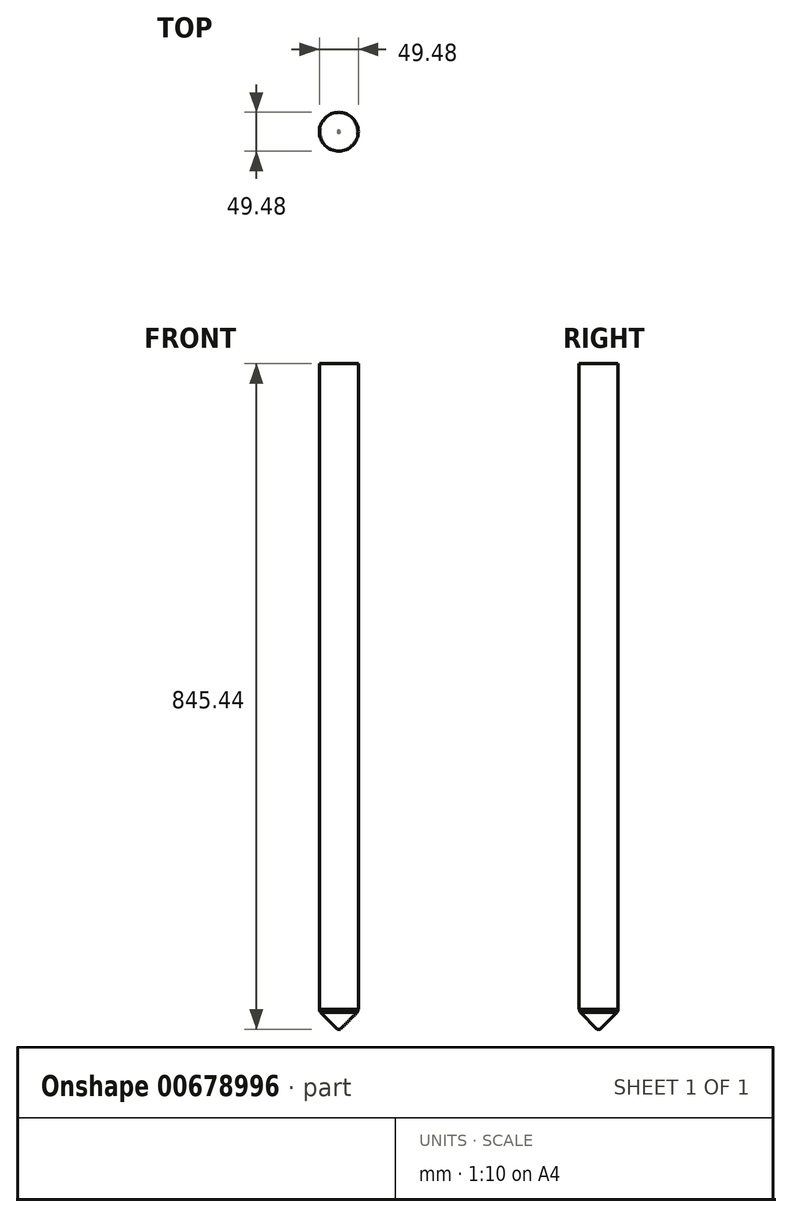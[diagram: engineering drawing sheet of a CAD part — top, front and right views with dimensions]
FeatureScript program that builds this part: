
annotation { "Feature Type Name" : "Feature", "Feature Type Description" : "" }
export const myFeature = defineFeature(function(context is Context, id is Id, definition is map)
    precondition{}
    {
        {
            var Q0;
            Q0=qCreatedBy(makeId("Front.planeOp"),FACE);
            var sketch = newSketch(context, id + "F0", { "sketchPlane" : qUnion([Q0])});
            skLineSegment(sketch, "E0", {"start": v(0, 179.46) * mm, "end": v(0, -240.34) * mm, "construction": true});
            skLineSegment(sketch, "E1.bottom", {"start": v(0, 179.46) * mm, "end": v(-24.74, 179.46) * mm});
            skLineSegment(sketch, "E1.top", {"start": v(0, -240.34) * mm, "end": v(-24.74, -240.34) * mm});
            skLineSegment(sketch, "E1.left", {"start": v(0, 179.46) * mm, "end": v(0, -240.34) * mm});
            skLineSegment(sketch, "E1.right", {"start": v(-24.74, 179.46) * mm, "end": v(-24.74, -240.34) * mm});
            skSolve(sketch);
        }
        {
            var Q0;
            Q0=makeQuery(id+"F0.imprint","IMPRINT",FACE,{"disambiguationData":[TD([[makeQuery(id+"F0.imprint","IMPRINT",EDGE,{"derivedFrom":sQuery(id+"F0.wireOp",EDGE,"E1.bottom")}),1.0]])]});
            var Q1;
            Q1=sQuery(id+"F0.wireOp",EDGE,"E1.left");
            revolve(context, id + "F1", {"entities" : qUnion([Q0]), "axis" : qUnion([Q1]), "revolveType" : RevolveType.FULL});
        }
        {
            var Q0;
            Q0=makeQuery(id+"F1.opRevolve","SWEPT_FACE",FACE,{"disambiguationData":[OSD([sQuery(id+"F0.wireOp",EDGE,"E1.top")])]});
            extrude(context, id + "F2", {"entities" : qUnion([Q0]), "operationType" : NewBodyOperationType.ADD, "depth" : 425.65 * mm, "offsetDistance" : 25.4 * mm});
        }
        {
            var Q0;
            Q0=makeQuery(id+"F2.opExtrude","CAP_EDGE",EDGE,{"disambiguationData":[OSD([sQuery(id+"F0.wireOp",EDGE,"E1.top"),sQuery(id+"F0.wireOp",EDGE,"E1.right")])],"isStart":false});
            chamfer(context, id + "F3", {"entities" : qUnion([Q0]), "width" : 22.86 * mm, "tangentPropagation" : true});
        }
        {
            var Q0;
            {var subQ0=sQuery(id+"F0.wireOp",EDGE,"E1.right");var subQ1=sQuery(id+"F0.wireOp",EDGE,"E1.top");Q0=makeQuery(id+"F3.opChamfer","BLEND_EDGE",EDGE,{"blendedFrom":[makeQuery(id+"F2.opExtrude","CAP_EDGE",EDGE,{"disambiguationData":[OSD([subQ1,subQ0])],"isStart":false}),makeQuery(id+"F2.boolean.opBoolean","MERGE",FACE,{"derivedFrom":[makeQuery(id+"F1.opRevolve","SWEPT_FACE",FACE,{"disambiguationData":[OSD([subQ0])]}),makeQuery(id+"F2.opExtrude","SWEPT_FACE",FACE,{"disambiguationData":[OSD([subQ1,subQ0])]})]})],"blendedInto":[makeQuery(id+"F2.boolean.opBoolean","MERGE",FACE,{"derivedFrom":[makeQuery(id+"F1.opRevolve","SWEPT_FACE",FACE,{"disambiguationData":[OSD([subQ0])]}),makeQuery(id+"F2.opExtrude","SWEPT_FACE",FACE,{"disambiguationData":[OSD([subQ1,subQ0])]})]})]});}
            chamfer(context, id + "F4", {"entities" : qUnion([Q0]), "width" : 5.08 * mm, "tangentPropagation" : true});
        }
        {
            var Q0;
            {var subQ0=sQuery(id+"F0.wireOp",EDGE,"E1.right");var subQ1=sQuery(id+"F0.wireOp",EDGE,"E1.top");var subQ2=makeQuery(id+"F2.boolean.opBoolean","MERGE",FACE,{"derivedFrom":[makeQuery(id+"F1.opRevolve","SWEPT_FACE",FACE,{"disambiguationData":[OSD([subQ0])]}),makeQuery(id+"F2.opExtrude","SWEPT_FACE",FACE,{"disambiguationData":[OSD([subQ1,subQ0])]})]});Q0=makeQuery(id+"F4.opChamfer","BLEND_EDGE",EDGE,{"blendedFrom":[makeQuery(id+"F3.opChamfer","BLEND_EDGE",EDGE,{"blendedFrom":[makeQuery(id+"F2.opExtrude","CAP_EDGE",EDGE,{"disambiguationData":[OSD([subQ1,subQ0])],"isStart":false}),subQ2],"blendedInto":[subQ2]}),subQ2],"blendedInto":[subQ2]});}
            chamfer(context, id + "F5", {"entities" : qUnion([Q0]), "width" : 2.54 * mm, "tangentPropagation" : true});
        }
    });
